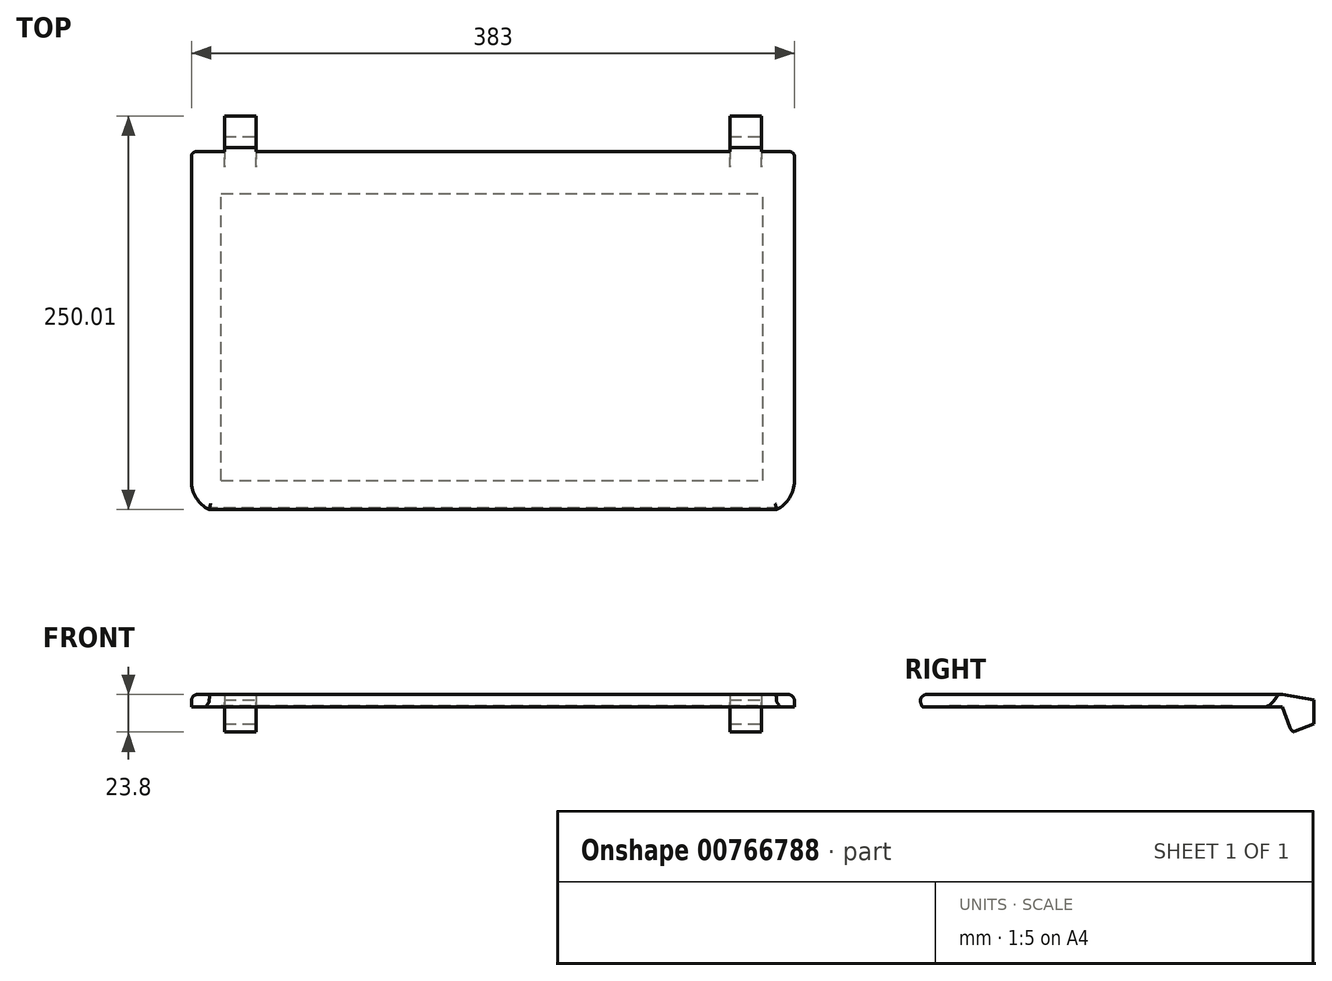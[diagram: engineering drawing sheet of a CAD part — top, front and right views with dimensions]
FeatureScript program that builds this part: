
annotation { "Feature Type Name" : "Feature", "Feature Type Description" : "" }
export const myFeature = defineFeature(function(context is Context, id is Id, definition is map)
    precondition{}
    {
        {
            var Q0;
            Q0=qCreatedBy(makeId("Top.planeOp"),FACE);
            var sketch = newSketch(context, id + "F0", { "sketchPlane" : qUnion([Q0])});
            skLineSegment(sketch, "E0.bottom", {"start": v(171.5, -126) * mm, "end": v(-171.5, -126) * mm});
            skLineSegment(sketch, "E0.top", {"start": v(171.5, 126) * mm, "end": v(-171.5, 126) * mm});
            skLineSegment(sketch, "E0.left", {"start": v(191.5, -106) * mm, "end": v(191.5, 106) * mm});
            skLineSegment(sketch, "E0.right", {"start": v(-191.5, -106) * mm, "end": v(-191.5, 106) * mm});
            skPoint(sketch, "E0.middle", {"position": v(0, 0) * mm});
            skPoint(sketch, "E1.visualSharp", {"position": v(191.5, -126) * mm});
            skArc(sketch, "E1.filletArc", {"start": v(171.5, -126) * mm, "mid": v(185.64, -120.14) * mm, "end": v(191.5, -106) * mm});
            skPoint(sketch, "E2.visualSharp", {"position": v(-191.5, -126) * mm});
            skArc(sketch, "E2.filletArc", {"start": v(-191.5, -106) * mm, "mid": v(-185.64, -120.14) * mm, "end": v(-171.5, -126) * mm});
            skPoint(sketch, "E3.visualSharp", {"position": v(-191.5, 126) * mm});
            skArc(sketch, "E3.filletArc", {"start": v(-171.5, 126) * mm, "mid": v(-185.64, 120.14) * mm, "end": v(-191.5, 106) * mm});
            skPoint(sketch, "E4.visualSharp", {"position": v(191.5, 126) * mm});
            skArc(sketch, "E4.filletArc", {"start": v(191.5, 106) * mm, "mid": v(185.64, 120.14) * mm, "end": v(171.5, 126) * mm});
            skLineSegment(sketch, "E5", {"start": v(-191.5, 106) * mm, "end": v(191.5, 106) * mm});
            skLineSegment(sketch, "E6", {"start": v(-171.5, 126) * mm, "end": v(-171.5, 106) * mm});
            skLineSegment(sketch, "E7", {"start": v(-170.5, 126) * mm, "end": v(-170.5, 106) * mm});
            skLineSegment(sketch, "E8", {"start": v(-150.5, 126) * mm, "end": v(-150.5, 106) * mm});
            skLineSegment(sketch, "E9", {"start": v(-149.5, 126) * mm, "end": v(-149.5, 106) * mm});
            skLineSegment(sketch, "E10", {"start": v(149.5, 126) * mm, "end": v(149.5, 106) * mm});
            skLineSegment(sketch, "E11", {"start": v(150.5, 126) * mm, "end": v(150.5, 106) * mm});
            skLineSegment(sketch, "E12", {"start": v(170.5, 126) * mm, "end": v(170.5, 106) * mm});
            skLineSegment(sketch, "E13", {"start": v(171.5, 126) * mm, "end": v(171.5, 106) * mm});
            skSolve(sketch);
        }
        {
            var Q0;
            {var subQ0=sQuery(id+"F0.wireOp",EDGE,"E7");Q0=makeQuery(id+"F0.imprint","IMPRINT",FACE,{"disambiguationData":[TD([[makeQuery(id+"F0.imprint","IMPRINT",EDGE,{"derivedFrom":subQ0}),1.0]])]});}
            var Q1;
            Q1=makeQuery(id+"F0.imprint","IMPRINT",FACE,{"disambiguationData":[TD([[makeQuery(id+"F0.imprint","IMPRINT",EDGE,{"derivedFrom":sQuery(id+"F0.wireOp",EDGE,"E0.bottom")}),-1.0]])]});
            var Q2;
            {var subQ0=sQuery(id+"F0.wireOp",EDGE,"E11");Q2=makeQuery(id+"F0.imprint","IMPRINT",FACE,{"disambiguationData":[TD([[makeQuery(id+"F0.imprint","IMPRINT",EDGE,{"derivedFrom":subQ0}),1.0]])]});}
            extrude(context, id + "F1", {"entities" : qUnion([Q0, Q1, Q2]), "depth" : 25 * mm, "offsetDistance" : 25 * mm});
        }
        {
            var Q0;
            Q0=qCreatedBy(makeId("Right.planeOp"),FACE);
            var sketch = newSketch(context, id + "F2", { "sketchPlane" : qUnion([Q0])});
            skLineSegment(sketch, "E14", {"start": v(-121.86, 15) * mm, "end": v(94.63, 15) * mm});
            skLineSegment(sketch, "E15", {"start": v(-121.86, 15) * mm, "end": v(-120.33, 11.3) * mm});
            skLineSegment(sketch, "E16", {"start": v(-120.33, 11.3) * mm, "end": v(-107.47, 3.57) * mm});
            skLineSegment(sketch, "E17", {"start": v(-94.59, 0) * mm, "end": v(106, 0) * mm});
            skLineSegment(sketch, "E18", {"start": v(-121.86, 25) * mm, "end": v(-121.86, 0) * mm});
            skLineSegment(sketch, "E19", {"start": v(-121.86, 25) * mm, "end": v(126, 25) * mm});
            skLineSegment(sketch, "E20", {"start": v(113.45, 1.44) * mm, "end": v(126, 6.47) * mm});
            skLineSegment(sketch, "E21", {"start": v(126, 6.47) * mm, "end": v(126, 21.47) * mm});
            skLineSegment(sketch, "E22", {"start": v(-121.86, 17) * mm, "end": v(93.64, 17) * mm});
            skPoint(sketch, "E23.visualSharp", {"position": v(-101.53, 0) * mm});
            skArc(sketch, "E23.filletArc", {"start": v(-107.47, 3.57) * mm, "mid": v(-101.27, 0.91) * mm, "end": v(-94.59, 0) * mm});
            skLineSegment(sketch, "E24", {"start": v(126, 21.47) * mm, "end": v(126, 25) * mm});
            skLineSegment(sketch, "E25", {"start": v(126, 6.47) * mm, "end": v(126, 0) * mm});
            skLineSegment(sketch, "E26", {"start": v(-121.86, 0) * mm, "end": v(-94.59, 0) * mm});
            skLineSegment(sketch, "E27", {"start": v(106, 25) * mm, "end": v(126, 21.47) * mm});
            skLineSegment(sketch, "E28", {"start": v(100.58, 17.93) * mm, "end": v(106, 25) * mm});
            skLineSegment(sketch, "E29", {"start": v(99.6, 19.93) * mm, "end": v(103.48, 25) * mm});
            skArc(sketch, "E30.filletArc", {"start": v(106, 0) * mm, "mid": v(109.8, 0.36) * mm, "end": v(113.45, 1.44) * mm});
            skLineSegment(sketch, "E31", {"start": v(-121.86, 0) * mm, "end": v(-126, 0) * mm});
            skLineSegment(sketch, "E32", {"start": v(-126, 0) * mm, "end": v(-126, 25) * mm});
            skLineSegment(sketch, "E33", {"start": v(-126, 25) * mm, "end": v(-121.86, 25) * mm});
            skLineSegment(sketch, "E34", {"start": v(103.48, 25) * mm, "end": v(106, 25) * mm});
            skArc(sketch, "E35", {"start": v(93.64, 17) * mm, "mid": v(96.96, 17.77) * mm, "end": v(99.6, 19.93) * mm});
            skArc(sketch, "E36", {"start": v(94.63, 15) * mm, "mid": v(97.95, 15.77) * mm, "end": v(100.58, 17.93) * mm});
            skLineSegment(sketch, "E37", {"start": v(106, 25) * mm, "end": v(106, 0) * mm});
            skLineSegment(sketch, "E38", {"start": v(106, 25) * mm, "end": v(106, 25) * mm});
            skLineSegment(sketch, "E39", {"start": v(-121.86, 17) * mm, "end": v(-122.69, 17) * mm});
            skLineSegment(sketch, "E40", {"start": v(126, 0) * mm, "end": v(106, 0) * mm});
            skLineSegment(sketch, "E41", {"start": v(-122.69, 17) * mm, "end": v(-126, 25) * mm});
            skSolve(sketch);
        }
        {
            var Q0;
            {var subQ0=sQuery(id+"F2.wireOp",EDGE,"E31");Q0=makeQuery(id+"F2.imprint","IMPRINT",FACE,{"disambiguationData":[TD([[makeQuery(id+"F2.imprint","IMPRINT",EDGE,{"derivedFrom":subQ0}),-1.0]])]});}
            var Q1;
            {var subQ1=sQuery(id+"F2.wireOp",EDGE,"E15");Q1=makeQuery(id+"F2.imprint","IMPRINT",FACE,{"disambiguationData":[TD([[makeQuery(id+"F2.imprint","IMPRINT",EDGE,{"derivedFrom":subQ1}),-1.0]])]});}
            var Q2;
            Q2=makeQuery(id+"F2.imprint","IMPRINT",FACE,{"disambiguationData":[TD([[makeQuery(id+"F2.imprint","IMPRINT",EDGE,{"derivedFrom":sQuery(id+"F2.wireOp",EDGE,"E20")}),-1.0]])]});
            var Q3;
            {var subQ2=sQuery(id+"F2.wireOp",EDGE,"E24");Q3=makeQuery(id+"F2.imprint","IMPRINT",FACE,{"disambiguationData":[TD([[makeQuery(id+"F2.imprint","IMPRINT",EDGE,{"derivedFrom":subQ2}),1.0]])]});}
            var Q4;
            {var subQ5=sQuery(id+"F2.wireOp",EDGE,"E14");Q4=makeQuery(id+"F2.imprint","IMPRINT",FACE,{"disambiguationData":[TD([[makeQuery(id+"F2.imprint","IMPRINT",EDGE,{"derivedFrom":subQ5}),1.0]])]});}
            var Q5;
            Q5=makeQuery(id+"F2.imprint","IMPRINT",FACE,{"disambiguationData":[TD([[makeQuery(id+"F2.imprint","IMPRINT",EDGE,{"derivedFrom":sQuery(id+"F2.wireOp",EDGE,"E14")}),-1.0]])]});
            var Q6;
            Q6=sQuery(id+"F2.wireOp",EDGE,"E27");
            var Q7;
            Q7=sQuery(id+"F2.wireOp",EDGE,"E24");
            var Q8;
            Q8=sQuery(id+"F2.wireOp",EDGE,"E19");
            var Q9;
            Q9=sQuery(id+"F2.wireOp",EDGE,"620c67eb-1812-4be7-8742-3993f2791620");
            var Q10;
            Q10=sQuery(id+"F2.wireOp",EDGE,"E30.filletArc");
            var Q11;
            Q11=sQuery(id+"F2.wireOp",EDGE,"E20");
            var Q12;
            Q12=sQuery(id+"F2.wireOp",EDGE,"E25");
            var Q13;
            Q13=sQuery(id+"F2.wireOp",EDGE,"E17");
            var Q14;
            Q14=sQuery(id+"F2.wireOp",EDGE,"e790bc0c-1d62-4571-abec-f0e13a19c521");
            var Q15;
            Q15=sQuery(id+"F2.wireOp",EDGE,"E14");
            var Q16;
            Q16=sQuery(id+"F2.wireOp",EDGE,"E28");
            var Q17;
            Q17=sQuery(id+"F2.wireOp",EDGE,"E36");
            var Q18;
            Q18=sQuery(id+"F2.wireOp",EDGE,"E32");
            var Q19;
            Q19=sQuery(id+"F2.wireOp",EDGE,"E15");
            var Q20;
            Q20=sQuery(id+"F2.wireOp",EDGE,"U2jdCMD3-jzvI-rudD-GJ9Q-Z8g9jYdM0oEz");
            var Q21;
            Q21=sQuery(id+"F2.wireOp",EDGE,"E18");
            var Q22;
            Q22=sQuery(id+"F2.wireOp",EDGE,"E16");
            var Q23;
            Q23=sQuery(id+"F2.wireOp",EDGE,"E26");
            var Q24;
            Q24=sQuery(id+"F2.wireOp",EDGE,"E31");
            var Q25;
            Q25=sQuery(id+"F2.wireOp",EDGE,"E23.filletArc");
            extrude(context, id + "F3", {"entities" : qUnion([Q0, Q1, Q2, Q3, Q4, Q5]), "operationType" : NewBodyOperationType.REMOVE, "surfaceEntities" : qUnion([Q6, Q7, Q8, Q9, Q10, Q11, Q12, Q13, Q14, Q15, Q16, Q17, Q18, Q19, Q20, Q21, Q22, Q23, Q24, Q25]), "oppositeDirection" : true, "depth" : 383 * mm, "offsetDistance" : 25 * mm, "symmetric" : true});
        }
        {
            var Q0;
            Q0=makeQuery(id+"F1.opExtrude","CAP_EDGE",EDGE,{"disambiguationData":[OSD([sQuery(id+"F0.wireOp",EDGE,"E0.left")])],"isStart":false});
            var Q1;
            Q1=makeQuery(id+"F1.opExtrude","CAP_EDGE",EDGE,{"disambiguationData":[OSD([sQuery(id+"F0.wireOp",EDGE,"E1.filletArc")])],"isStart":false});
            var Q2;
            Q2=makeQuery(id+"F3.boolean.opBoolean","MERGE",EDGE,{"derivedFrom":[makeQuery(id+"F1.opExtrude","CAP_EDGE",EDGE,{"disambiguationData":[OSD([sQuery(id+"F0.wireOp",EDGE,"E0.bottom")])],"isStart":false})],"fromTools":[makeQuery(id+"F3.opExtrude","SWEPT_EDGE",EDGE,{"disambiguationData":[OSD([sQuery(id+"F2.wireOp",EDGE,"E32"),sQuery(id+"F2.wireOp",EDGE,"E33"),sQuery(id+"F2.wireOp",EDGE,"E41")])]})]});
            var Q3;
            Q3=makeQuery(id+"F1.opExtrude","CAP_EDGE",EDGE,{"disambiguationData":[OSD([sQuery(id+"F0.wireOp",EDGE,"E0.right")])],"isStart":false});
            var Q4;
            Q4=makeQuery(id+"F1.opExtrude","CAP_EDGE",EDGE,{"disambiguationData":[OSD([sQuery(id+"F0.wireOp",EDGE,"E2.filletArc")])],"isStart":false});
            fillet(context, id + "F4", {"entities" : qUnion([Q0, Q1, Q2, Q3, Q4]), "tangentPropagation" : true, "radius" : 4 * mm, "defaultsChanged" : true, "vertexSettings" : [], "allowEdgeOverflow" : false});
        }
        {
            var Q0;
            Q0=qCreatedBy(makeId("Front.planeOp"),FACE);
            var sketch = newSketch(context, id + "F5", { "sketchPlane" : qUnion([Q0])});
            skLineSegment(sketch, "E42", {"start": v(-170.5, 17) * mm, "end": v(-170.5, 25) * mm});
            skLineSegment(sketch, "E43", {"start": v(-170.5, 25) * mm, "end": v(-150.5, 25) * mm});
            skLineSegment(sketch, "E44", {"start": v(-150.5, 25) * mm, "end": v(-150.5, 17) * mm});
            skLineSegment(sketch, "E45", {"start": v(-150.5, 17) * mm, "end": v(-170.5, 17) * mm});
            skLineSegment(sketch, "E46", {"start": v(150.5, 17) * mm, "end": v(150.5, 25) * mm});
            skLineSegment(sketch, "E47", {"start": v(150.5, 25) * mm, "end": v(170.5, 25) * mm});
            skLineSegment(sketch, "E48", {"start": v(170.5, 25) * mm, "end": v(170.5, 17) * mm});
            skLineSegment(sketch, "E49", {"start": v(170.5, 17) * mm, "end": v(150.5, 17) * mm});
            skSolve(sketch);
        }
        {
            var Q0;
            Q0 = qSketchRegion(id + "F5", true);
            extrude(context, id + "F6", {"entities" : qUnion([Q0]), "operationType" : NewBodyOperationType.ADD, "oppositeDirection" : true, "depth" : 106 * mm, "offsetDistance" : 25 * mm});
        }
        {
            var Q0;
            Q0=makeQuery(id+"F6.boolean.opBoolean","MERGE",FACE,{"derivedFrom":[makeQuery(id+"F3.boolean.opBoolean","COPY",FACE,{"derivedFrom":makeQuery(id+"F3.opExtrude","SWEPT_FACE",FACE,{"disambiguationData":[OSD([sQuery(id+"F2.wireOp",EDGE,"E22"),sQuery(id+"F2.wireOp",EDGE,"E39")])]})}),makeQuery(id+"F6.opExtrude","SWEPT_FACE",FACE,{"disambiguationData":[OSD([sQuery(id+"F5.wireOp",EDGE,"E45")])]}),makeQuery(id+"F6.opExtrude","SWEPT_FACE",FACE,{"disambiguationData":[OSD([sQuery(id+"F5.wireOp",EDGE,"E49")])]})]});
            var sketch = newSketch(context, id + "F7", { "sketchPlane" : qUnion([Q0])});
            skLineSegment(sketch, "E50.bottom", {"start": v(-172.5, 105.69) * mm, "end": v(171.5, 105.69) * mm});
            skLineSegment(sketch, "E50.top", {"start": v(-172.5, -76.64) * mm, "end": v(171.5, -76.64) * mm});
            skLineSegment(sketch, "E50.left", {"start": v(-172.5, 105.69) * mm, "end": v(-172.5, -76.64) * mm});
            skLineSegment(sketch, "E50.right", {"start": v(171.5, 105.69) * mm, "end": v(171.5, -76.64) * mm});
            skSolve(sketch);
        }
        {
            var Q0;
            Q0 = qSketchRegion(id + "F7", true);
            extrude(context, id + "F8", {"entities" : qUnion([Q0]), "operationType" : NewBodyOperationType.REMOVE, "oppositeDirection" : true, "depth" : 1 * mm, "offsetDistance" : 25 * mm});
        }
        {
            var Q0;
            Q0=makeQuery(id+"F1.opExtrude","SWEPT_FACE",FACE,{"disambiguationData":[OSD([sQuery(id+"F0.wireOp",EDGE,"E12")])]});
            var sketch = newSketch(context, id + "F9", { "sketchPlane" : qUnion([Q0])});
            skLineSegment(sketch, "E51", {"start": v(114.04, 0) * mm, "end": v(111.92, 2.12) * mm});
            skLineSegment(sketch, "E52", {"start": v(110.75, 3.95) * mm, "end": v(106, 17) * mm});
            skLineSegment(sketch, "E53", {"start": v(106, 17) * mm, "end": v(106, 0) * mm});
            skLineSegment(sketch, "E54", {"start": v(106, 0) * mm, "end": v(114.04, 0) * mm});
            skPoint(sketch, "E55.visualSharp", {"position": v(111.13, 2.9) * mm});
            skArc(sketch, "E55.filletArc", {"start": v(110.75, 3.95) * mm, "mid": v(111.23, 2.97) * mm, "end": v(111.92, 2.12) * mm});
            skSolve(sketch);
        }
        {
            var Q0;
            Q0 = qSketchRegion(id + "F9", true);
            extrude(context, id + "F10", {"entities" : qUnion([Q0]), "operationType" : NewBodyOperationType.REMOVE, "oppositeDirection" : true, "depth" : 383 * mm, "offsetDistance" : 25 * mm});
        }
    });
